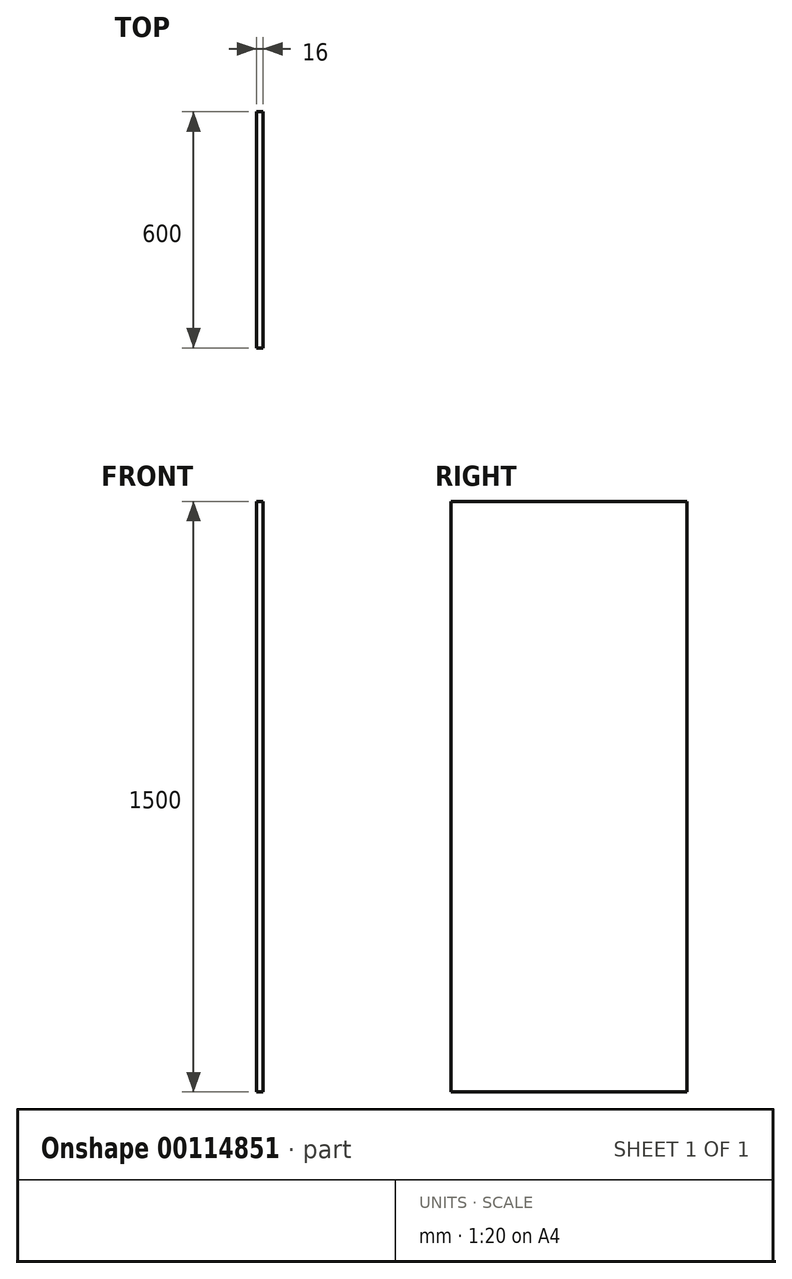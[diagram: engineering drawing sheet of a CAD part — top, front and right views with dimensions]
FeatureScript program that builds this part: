
annotation { "Feature Type Name" : "Feature", "Feature Type Description" : "" }
export const myFeature = defineFeature(function(context is Context, id is Id, definition is map)
    precondition{}
    {
        {
            var Q0;
            Q0=qCreatedBy(makeId("Right.planeOp"),FACE);
            var sketch = newSketch(context, id + "F0", { "sketchPlane" : qUnion([Q0])});
            skLineSegment(sketch, "E0.bottom", {"start": v(-300, 750) * mm, "end": v(300, 750) * mm});
            skLineSegment(sketch, "E0.top", {"start": v(-300, -750) * mm, "end": v(300, -750) * mm});
            skLineSegment(sketch, "E0.left", {"start": v(-300, 750) * mm, "end": v(-300, -750) * mm});
            skLineSegment(sketch, "E0.right", {"start": v(300, 750) * mm, "end": v(300, -750) * mm});
            skPoint(sketch, "E0.middle", {"position": v(0, 0) * mm});
            skSolve(sketch);
        }
        {
            var Q0;
            Q0=makeQuery(id+"F0.imprint","IMPRINT",FACE,{"disambiguationData":[TD([[makeQuery(id+"F0.imprint","IMPRINT",EDGE,{"derivedFrom":sQuery(id+"F0.wireOp",EDGE,"E0.bottom")}),-1.0]])]});
            extrude(context, id + "F1", {"entities" : qUnion([Q0]), "endBound" : BoundingType.SYMMETRIC, "depth" : 16 * mm});
        }
    });
